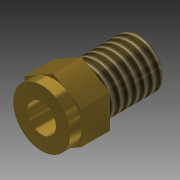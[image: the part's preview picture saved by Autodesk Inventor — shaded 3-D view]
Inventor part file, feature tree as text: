
AUTODESK INVENTOR PART (.ipt)
format: ipt  version: 2011 (Build 150239000, 239)  size: 117,760 bytes
history: native  units: in
note: dims shown in document units (in); Inventor stores cm internally (conversion verified against a paired STEP export)
features: extrude x4, sketch x4, thread x1
ambient origin geometry x8: Origin, YZ Plane, XZ Plane, XY Plane, X Axis, Y Axis, Z Axis, Center Point
bodies: Solid1 (feature_tree)
feature tree (9):
  extrude  "Extrusion1"  Depth=0.5in TaperAngle=0.0deg
  thread  "Thread1"  [1 undecoded]
  extrude  "Extrusion2"  TaperAngle=0.0deg  [1 undecoded]
  extrude  "Extrusion3"  Depth=0.1in TaperAngle=0.0deg
  extrude  "Extrusion4"  Depth=0.1in TaperAngle=0.0deg
  sketch  "Sketch1"  dims[d0=0.425in d1=0.5in d2=0.0in d3=1.0in d4=0.0in]
  sketch  "Sketch2"  dims[d5=0.5in d6=0.0in]
  sketch  "Sketch3"  dims[d7=0.25in d8=0.0in d9=0.1in d10=0.0in]
  sketch  "Sketch4"  dims[d11=0.25in d12=0.1in d13=0.0in]
note: 2 required parameter values undecoded (feature->parameter linkage not recoverable at this tier; creation-order binding heuristic only, values carry confidence <= 0.55)
